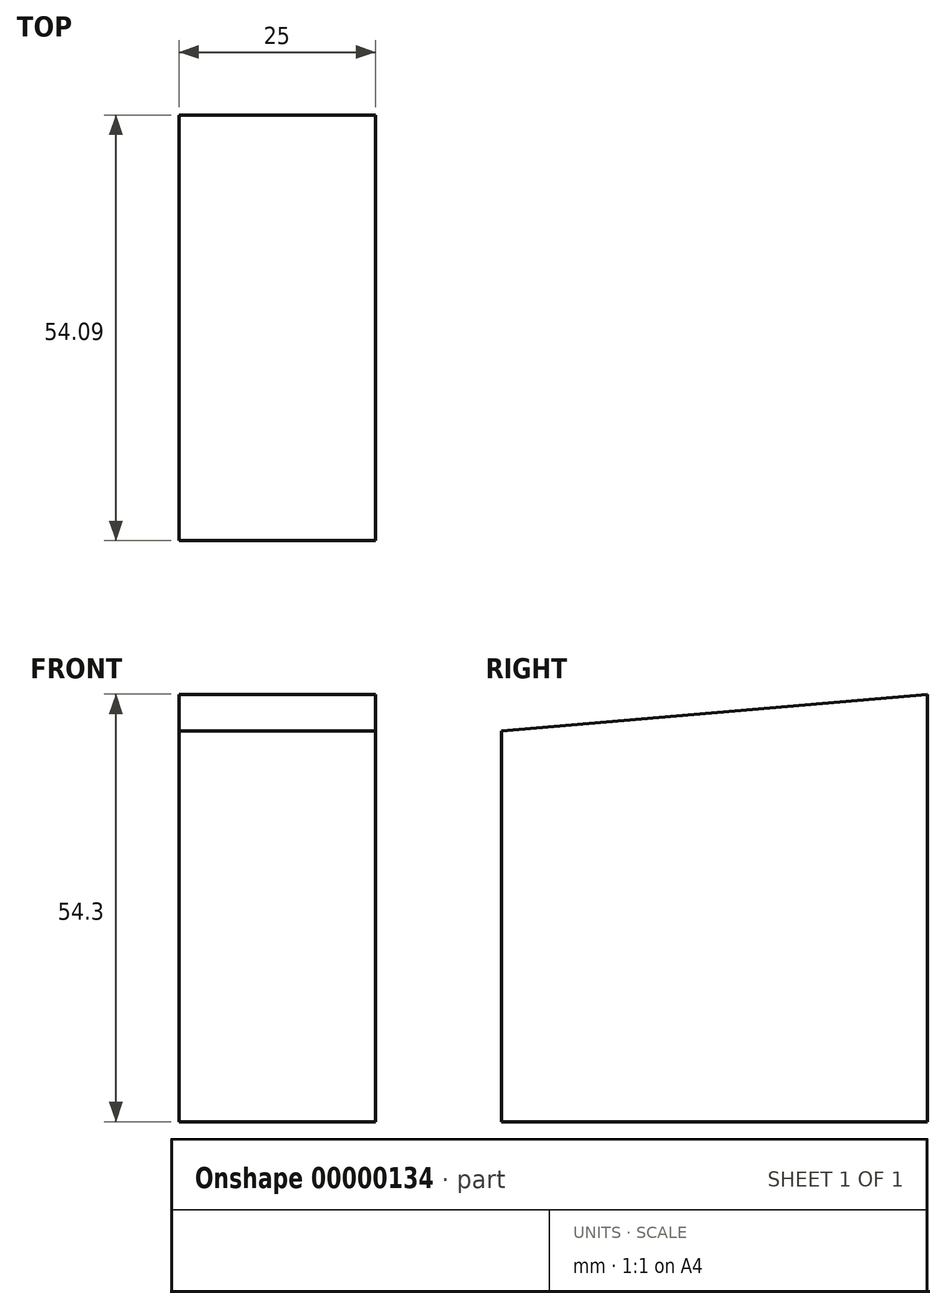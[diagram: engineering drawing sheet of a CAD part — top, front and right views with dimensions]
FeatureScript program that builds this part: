
annotation { "Feature Type Name" : "Feature", "Feature Type Description" : "" }
export const myFeature = defineFeature(function(context is Context, id is Id, definition is map)
    precondition{}
    {
        {
            var Q0;
            Q0=qCreatedBy(makeId("Right.planeOp"),FACE);
            var sketch = newSketch(context, id + "F0", { "sketchPlane" : qUnion([Q0])});
            skLineSegment(sketch, "E0.bottom", {"start": v(-30.56, 23.16) * mm, "end": v(23.53, 27.85) * mm});
            skLineSegment(sketch, "E0.top", {"start": v(-30.56, -26.45) * mm, "end": v(23.53, -26.45) * mm});
            skLineSegment(sketch, "E0.left", {"start": v(-30.56, 23.16) * mm, "end": v(-30.56, -26.45) * mm});
            skLineSegment(sketch, "E0.right", {"start": v(23.53, 27.85) * mm, "end": v(23.53, -26.45) * mm});
            skSolve(sketch);
        }
        {
            var Q0;
            Q0=makeQuery(id+"F0.imprint","IMPRINT",FACE,{"disambiguationData":[TD([[makeQuery(id+"F0.imprint","IMPRINT",EDGE,{"derivedFrom":sQuery(id+"F0.wireOp",EDGE,"E0.bottom")}),-1.0]])]});
            extrude(context, id + "F1", {"entities" : qUnion([Q0]), "depth" : 25 * mm});
        }
    });
